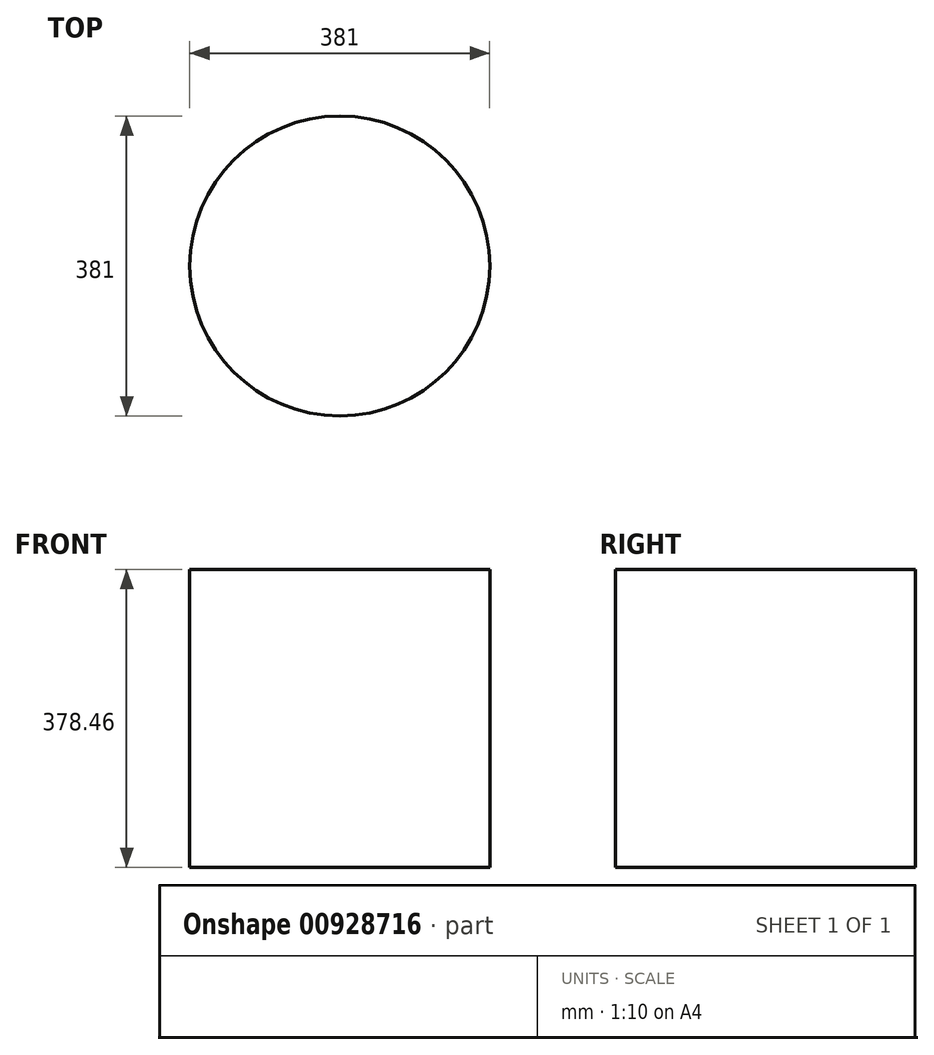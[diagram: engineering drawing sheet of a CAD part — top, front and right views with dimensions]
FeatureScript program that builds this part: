
annotation { "Feature Type Name" : "Feature", "Feature Type Description" : "" }
export const myFeature = defineFeature(function(context is Context, id is Id, definition is map)
    precondition{}
    {
        {
            var Q0;
            Q0=qCreatedBy(makeId("Top.planeOp"),FACE);
            var sketch = newSketch(context, id + "F0", { "sketchPlane" : qUnion([Q0])});
            skCircle(sketch, "E0", {"center": v(-52.15, 52.4) * mm, "radius": 190.5 * mm});
            skSolve(sketch);
        }
        {
            var Q0;
            Q0=makeQuery(id+"F0.imprint","IMPRINT",FACE,{"disambiguationData":[TD([[makeQuery(id+"F0.imprint","IMPRINT",EDGE,{"derivedFrom":sQuery(id+"F0.wireOp",EDGE,"E0")}),1.0]])]});
            extrude(context, id + "F1", {"entities" : qUnion([Q0]), "depth" : 378.46 * mm, "offsetDistance" : 25.4 * mm});
        }
        {
            var Q0;
            Q0=makeQuery(id+"F1.opExtrude","CAP_FACE",FACE,{"disambiguationData":[OSD([sQuery(id+"F0.wireOp",EDGE,"E0")])],"isStart":false});
            var sketch = newSketch(context, id + "F2", { "sketchPlane" : qUnion([Q0])});
            skLineSegment(sketch, "E1", {"start": v(0, 99.67) * mm, "end": v(-135.52, 127.4) * mm});
            skLineSegment(sketch, "E2", {"start": v(-135.52, 127.4) * mm, "end": v(-135.52, 58.76) * mm});
            skLineSegment(sketch, "E3", {"start": v(-135.52, 58.76) * mm, "end": v(0, 99.67) * mm});
            skSolve(sketch);
        }
    });
